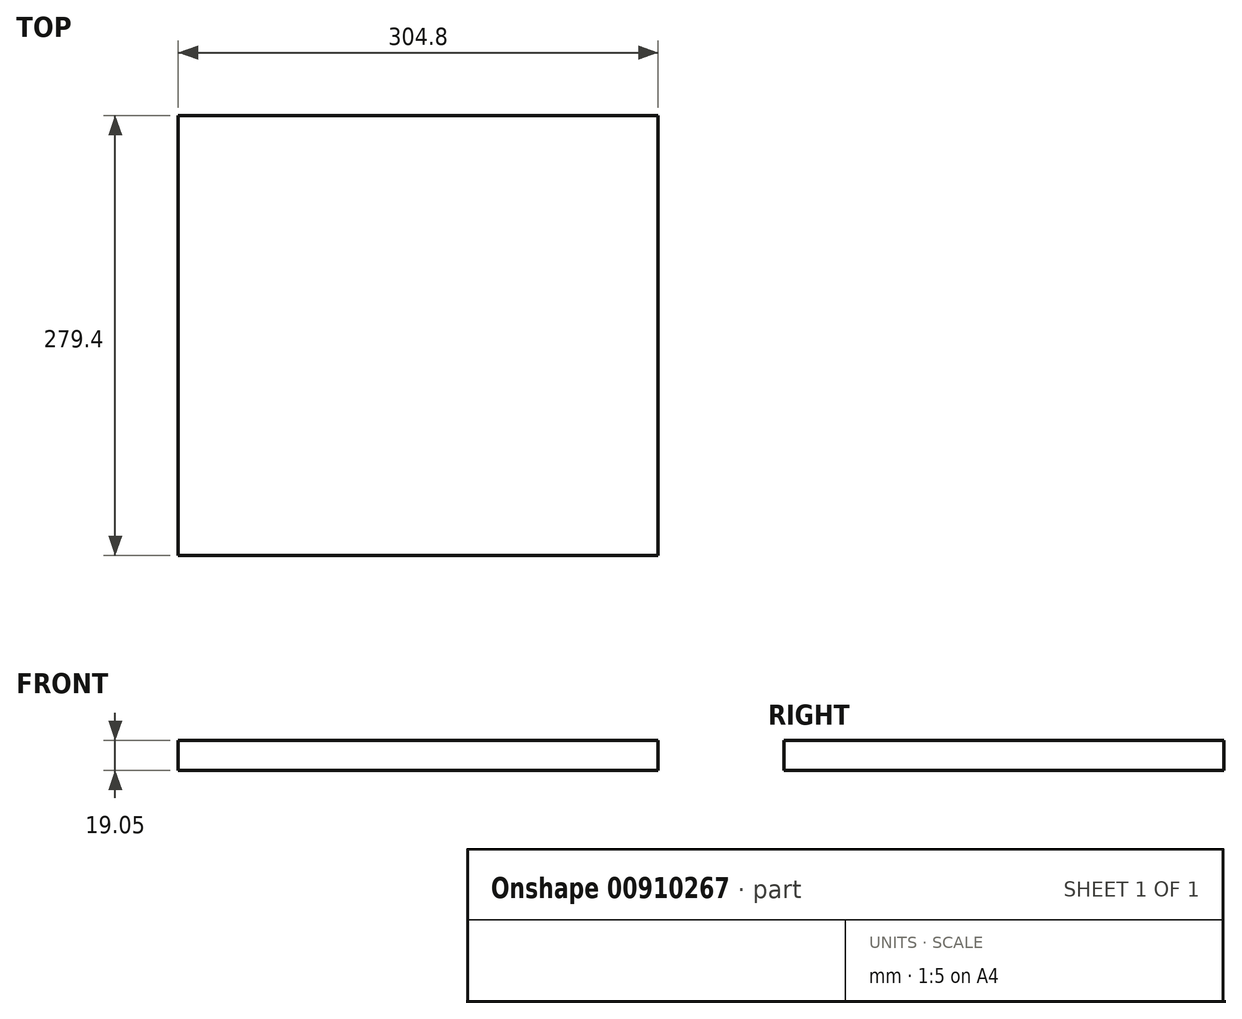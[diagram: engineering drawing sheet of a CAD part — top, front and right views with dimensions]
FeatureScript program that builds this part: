
annotation { "Feature Type Name" : "Feature", "Feature Type Description" : "" }
export const myFeature = defineFeature(function(context is Context, id is Id, definition is map)
    precondition{}
    {
        {
            var Q0;
            Q0=qCreatedBy(makeId("Top.planeOp"),FACE);
            var sketch = newSketch(context, id + "F0", { "sketchPlane" : qUnion([Q0])});
            skLineSegment(sketch, "E0.bottom", {"start": v(152.4, 139.7) * mm, "end": v(-152.4, 139.7) * mm});
            skLineSegment(sketch, "E0.top", {"start": v(152.4, -139.7) * mm, "end": v(-152.4, -139.7) * mm});
            skLineSegment(sketch, "E0.left", {"start": v(152.4, 139.7) * mm, "end": v(152.4, -139.7) * mm});
            skLineSegment(sketch, "E0.right", {"start": v(-152.4, 139.7) * mm, "end": v(-152.4, -139.7) * mm});
            skPoint(sketch, "E0.middle", {"position": v(0, 0) * mm});
            skSolve(sketch);
        }
        {
            var Q0;
            Q0 = qSketchRegion(id + "F0", true);
            extrude(context, id + "F1", {"entities" : qUnion([Q0]), "depth" : 19.05 * mm, "offsetDistance" : 25.4 * mm});
        }
    });
